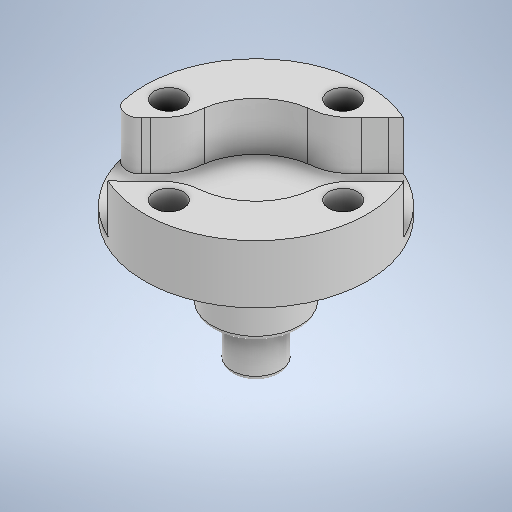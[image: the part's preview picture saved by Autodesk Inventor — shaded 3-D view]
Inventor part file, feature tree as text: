
AUTODESK INVENTOR PART (.ipt)
format: ipt  version: 2025.1 (Build 291241000, 241)  size: 424,448 bytes
history: native  units: in
note: dims shown in document units (in); Inventor stores cm internally (conversion verified against a paired STEP export)
features: extrude x7, sketch x7, fillet x4
ambient origin geometry x8: Origin, YZ Plane, XZ Plane, XY Plane, X Axis, Y Axis, Z Axis, Center Point
bodies: Solid1 (feature_tree)
feature tree (18):
  extrude  "Extrusion1"  Depth=0.1969in
  extrude  "Extrusion2"  Depth=0.315in TaperAngle=0.0deg
  extrude  "Extrusion3"  Depth=0.1969in
  extrude  "Extrusion4"  Depth=0.2362in
  extrude  "Extrusion5"  Depth=0.3543in
  extrude  "Extrusion7"  Depth=0.1181in
  extrude  "Extrusion8"  Depth=0.0197in
  fillet  "Fillet1"  Radius=0.1181in
  fillet  "Fillet2"  Radius=0.2362in
  fillet  "Fillet3"  Radius=0.1969in
  fillet  "Fillet4"  Radius=0.1969in
  sketch  "Sketch1"  dims[d0=1.0in d1=1.0in d2=2.0in d3=2.0in d4=0.4331in d5=0.4331in d6=0.4331in d7=0.4331in d8=0.4331in d9=0.4331in d10=0.4331in d11=0.4331in d12=0.4331in d13=2.7559in d14=0.1969in d15=0.1969in d16=0.8268in]
  sketch  "Sketch2"  dims[d17=0.5118in d18=0.315in d19=0.0in]
  sketch  "Sketch3"  dims[d20=1.0in d21=1.0in d22=2.0in d23=2.0in d24=0.4331in d25=0.4331in d26=0.4331in d27=0.4331in d28=0.4331in d29=0.4331in d30=0.4331in d31=0.4331in d32=0.4331in d33=2.7559in d34=0.1969in d35=0.1969in d36=0.9055in]
  sketch  "Sketch4"  dims[d37=0.2362in d38=0.0in d39=0.3543in]
  sketch  "Sketch5"  dims[d40=0.3543in d41=0.3543in]
  sketch  "Sketch8"  dims[d42=0.3543in d43=0.1181in]
  sketch  "Sketch9"  dims[d44=0.1181in d45=0.1181in d46=0.1181in d47=0.2362in d48=0.0in d49=0.1969in d50=0.1969in d51=0.0in d52=0.3543in d53=0.4724in d54=0.0in d71=0.1969in d72=0.0in d73=0.1969in d74=0.0in d75=0.2662in d76=0.0591in d77=0.0591in d78=0.0197in]
